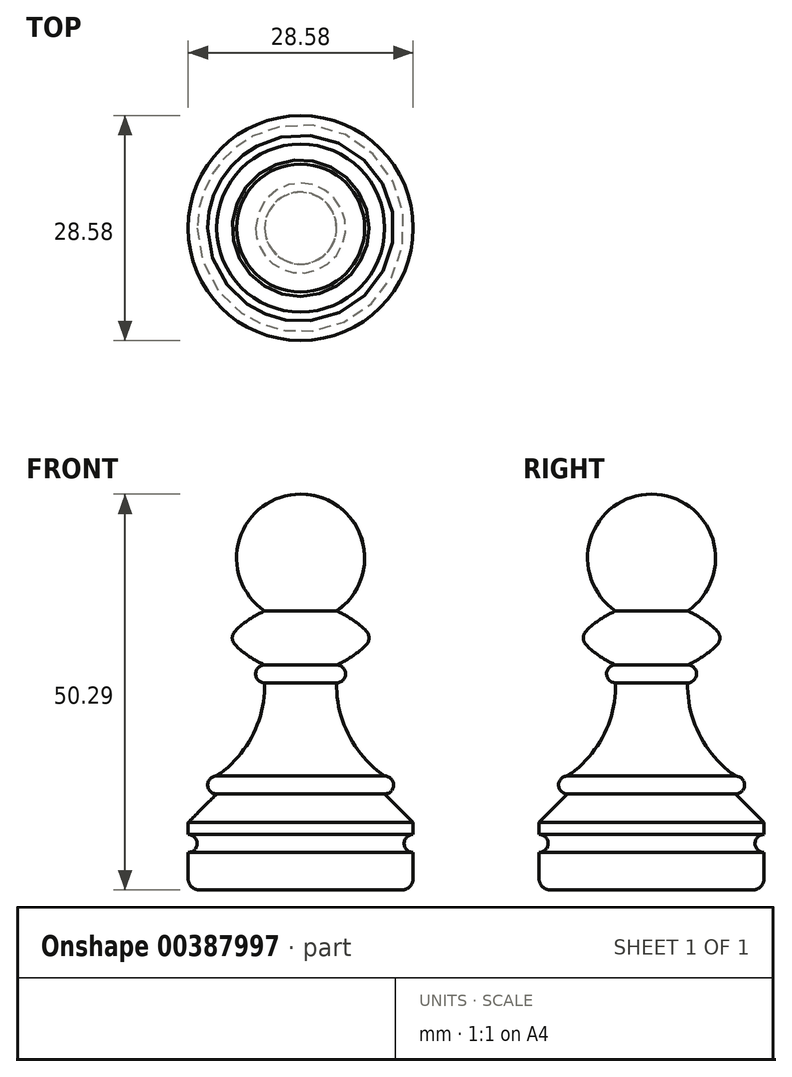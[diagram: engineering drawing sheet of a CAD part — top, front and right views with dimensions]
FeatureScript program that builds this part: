
annotation { "Feature Type Name" : "Feature", "Feature Type Description" : "" }
export const myFeature = defineFeature(function(context is Context, id is Id, definition is map)
    precondition{}
    {
        {
            var Q0;
            Q0=qCreatedBy(makeId("Front.planeOp"),FACE);
            var sketch = newSketch(context, id + "F0", { "sketchPlane" : qUnion([Q0])});
            skLineSegment(sketch, "E0", {"start": v(0, 0) * mm, "end": v(10.67, 0) * mm});
            skLineSegment(sketch, "E1", {"start": v(10.67, 0) * mm, "end": v(14.29, -3.62) * mm});
            skLineSegment(sketch, "E2", {"start": v(14.29, -3.62) * mm, "end": v(14.29, -5.14) * mm});
            skArc(sketch, "E3", {"start": v(14.29, -5.14) * mm, "mid": v(13.14, -6.29) * mm, "end": v(14.29, -7.43) * mm});
            skLineSegment(sketch, "E4", {"start": v(14.29, -7.43) * mm, "end": v(14.29, -12.2) * mm});
            skLineSegment(sketch, "E5", {"start": v(14.29, -12.2) * mm, "end": v(0, -12.2) * mm});
            skLineSegment(sketch, "E6", {"start": v(0, -12.2) * mm, "end": v(0, 0) * mm});
            skSolve(sketch);
        }
        {
            var Q0;
            Q0=makeQuery(id+"F0.imprint","IMPRINT",FACE,{"disambiguationData":[TD([[makeQuery(id+"F0.imprint","IMPRINT",EDGE,{"derivedFrom":sQuery(id+"F0.wireOp",EDGE,"E0")}),-1.0]])]});
            var Q1;
            Q1=sQuery(id+"F0.wireOp",EDGE,"E6");
            revolve(context, id + "F1", {"entities" : qUnion([Q0]), "axis" : qUnion([Q1]), "revolveType" : RevolveType.FULL});
        }
        {
            var Q0;
            Q0=makeQuery(id+"F1.opRevolve","SWEPT_EDGE",EDGE,{"disambiguationData":[OSD([sQuery(id+"F0.wireOp",EDGE,"E4"),sQuery(id+"F0.wireOp",EDGE,"E5")])]});
            fillet(context, id + "F2", {"entities" : qUnion([Q0]), "radius" : 1.43 * mm, "tangentPropagation" : true, "defaultsChanged" : true, "vertexSettings" : [], "allowEdgeOverflow" : false});
        }
        {
            var Q0;
            Q0=qCreatedBy(makeId("Front.planeOp"),FACE);
            var sketch = newSketch(context, id + "F3", { "sketchPlane" : qUnion([Q0])});
            skLineSegment(sketch, "E7", {"start": v(10.67, 0) * mm, "end": v(0, 0) * mm});
            skLineSegment(sketch, "E8", {"start": v(0, 0) * mm, "end": v(0, 38.1) * mm});
            skArc(sketch, "E9", {"start": v(4.57, 23.25) * mm, "mid": v(7.77, 32.36) * mm, "end": v(0, 38.1) * mm});
            skArc(sketch, "E10", {"start": v(4.57, 14.1) * mm, "mid": v(5.72, 15.25) * mm, "end": v(4.57, 16.4) * mm});
            skArc(sketch, "E11", {"start": v(4.57, 14.1) * mm, "mid": v(6.12, 7.42) * mm, "end": v(10.67, 2.29) * mm});
            skArc(sketch, "E12", {"start": v(10.67, 0) * mm, "mid": v(11.81, 1.14) * mm, "end": v(10.67, 2.29) * mm});
            skArc(sketch, "E13", {"start": v(9.14, 19.82) * mm, "mid": v(7.05, 21.8) * mm, "end": v(4.57, 23.25) * mm});
            skArc(sketch, "E14", {"start": v(4.57, 16.4) * mm, "mid": v(7.05, 17.85) * mm, "end": v(9.14, 19.82) * mm});
            skLineSegment(sketch, "E15", {"start": v(4.57, 23.25) * mm, "end": v(4.57, 16.4) * mm, "construction": true});
            skLineSegment(sketch, "E16", {"start": v(9.14, 19.82) * mm, "end": v(4.57, 19.82) * mm, "construction": true});
            skSolve(sketch);
        }
        {
            var Q0;
            Q0 = qSketchRegion(id + "F3", true);
            var Q1;
            Q1=sQuery(id+"F3.wireOp",EDGE,"E8");
            revolve(context, id + "F4", {"operationType" : NewBodyOperationType.ADD, "entities" : qUnion([Q0]), "axis" : qUnion([Q1]), "revolveType" : RevolveType.FULL});
        }
        {
            var Q0;
            Q0=makeQuery(id+"F4.opRevolve","SWEPT_EDGE",EDGE,{"disambiguationData":[OSD([sQuery(id+"F3.wireOp",EDGE,"E13"),sQuery(id+"F3.wireOp",EDGE,"E14")])]});
            fillet(context, id + "F5", {"entities" : qUnion([Q0]), "radius" : 1.27 * mm, "tangentPropagation" : true, "allowEdgeOverflow" : false});
        }
    });
